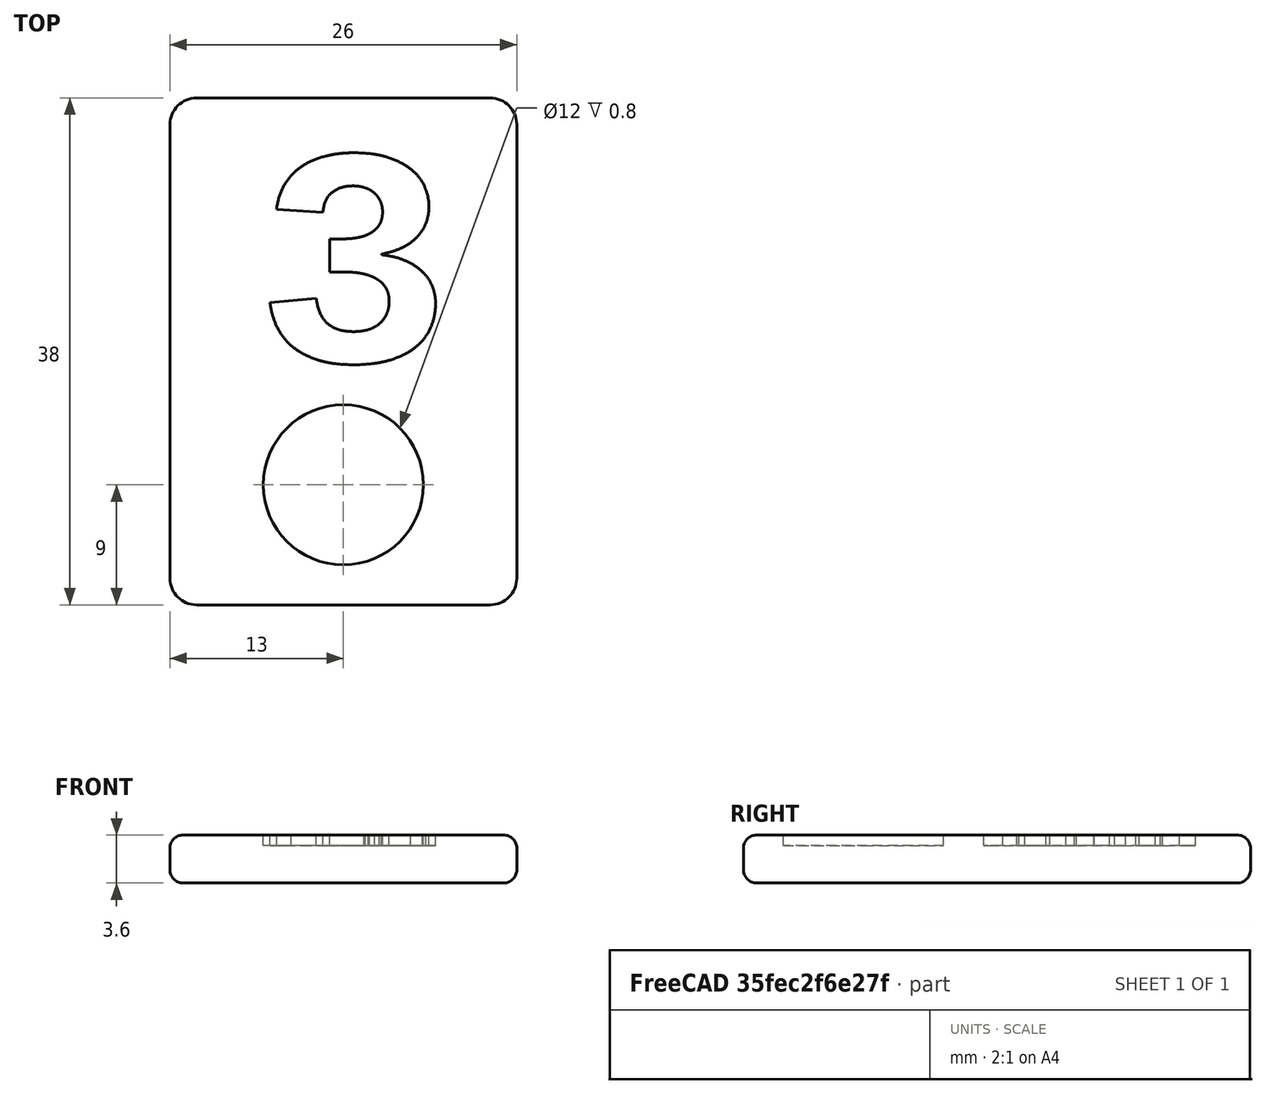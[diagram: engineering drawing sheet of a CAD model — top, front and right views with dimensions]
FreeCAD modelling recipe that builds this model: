
FCSTD DOCUMENT  (FreeCAD 0.14R3702 (Git))
Label: ficha3
License: CC-BY 3.0
LicenseURL: http://creativecommons.org/licenses/by/3.0/
objects: Part::Fillet×2, Part::Cut×2, Part::Box×1, Part::Part2DObjectPython×1, Part::Cylinder×1, Part::Extrusion×1
note: 8 computed .brp shape members not serialized (recipe doc carries the construction recipe); baked Part::Feature solids carry a one-line shape summary decoded from their .brp

FEATURE [Part::Box] Box  label="Cubo"
  Height = 3.6
  Length = 26
  Width = 38
FEATURE [Part::Fillet] Fillet
  Base = -> Box
  Edges = 4 edges r=2: [Edge1,Edge3,Edge5,Edge7]
FEATURE [Part::Part2DObjectPython] ShapeString  # Draft 2D object (typed FeaturePython)
  FontFile = <path>
  Placement = pos=(6.5,18,4) rot=(0,0,1;0rad)
  Size = 18
  String = 3
  Tracking = 0
FEATURE [Part::Cylinder] Cylinder  label="Cilindro"
  Angle = 360
  Height = 10
  Placement = pos=(13,9,2.8) rot=(0,0,1;0rad)
  Radius = 6
FEATURE [Part::Extrusion] Extrude001
  Base = -> ShapeString
  Dir = (0,0,2)
  Placement = pos=(0,0,-1.2) rot=(0,0,1;0rad)
  Solid = true
FEATURE [Part::Cut] Cut
  Base = -> Fillet
  Tool = -> Cylinder
FEATURE [Part::Cut] Cut001
  Base = -> Cut
  Tool = -> Extrude001
FEATURE [Part::Fillet] Fillet001
  Base = -> Cut001
  Edges = 16 edges r=1: [Edge1,Edge4,Edge59,Edge60,Edge61,Edge62,Edge63,Edge64,Edge65,Edge66,Edge68,Edge70,Edge71,Edge72,Edge73,Edge74]
note: 1 file-system path scrubbed to <path> (originals preserved in the JSON sidecar)
